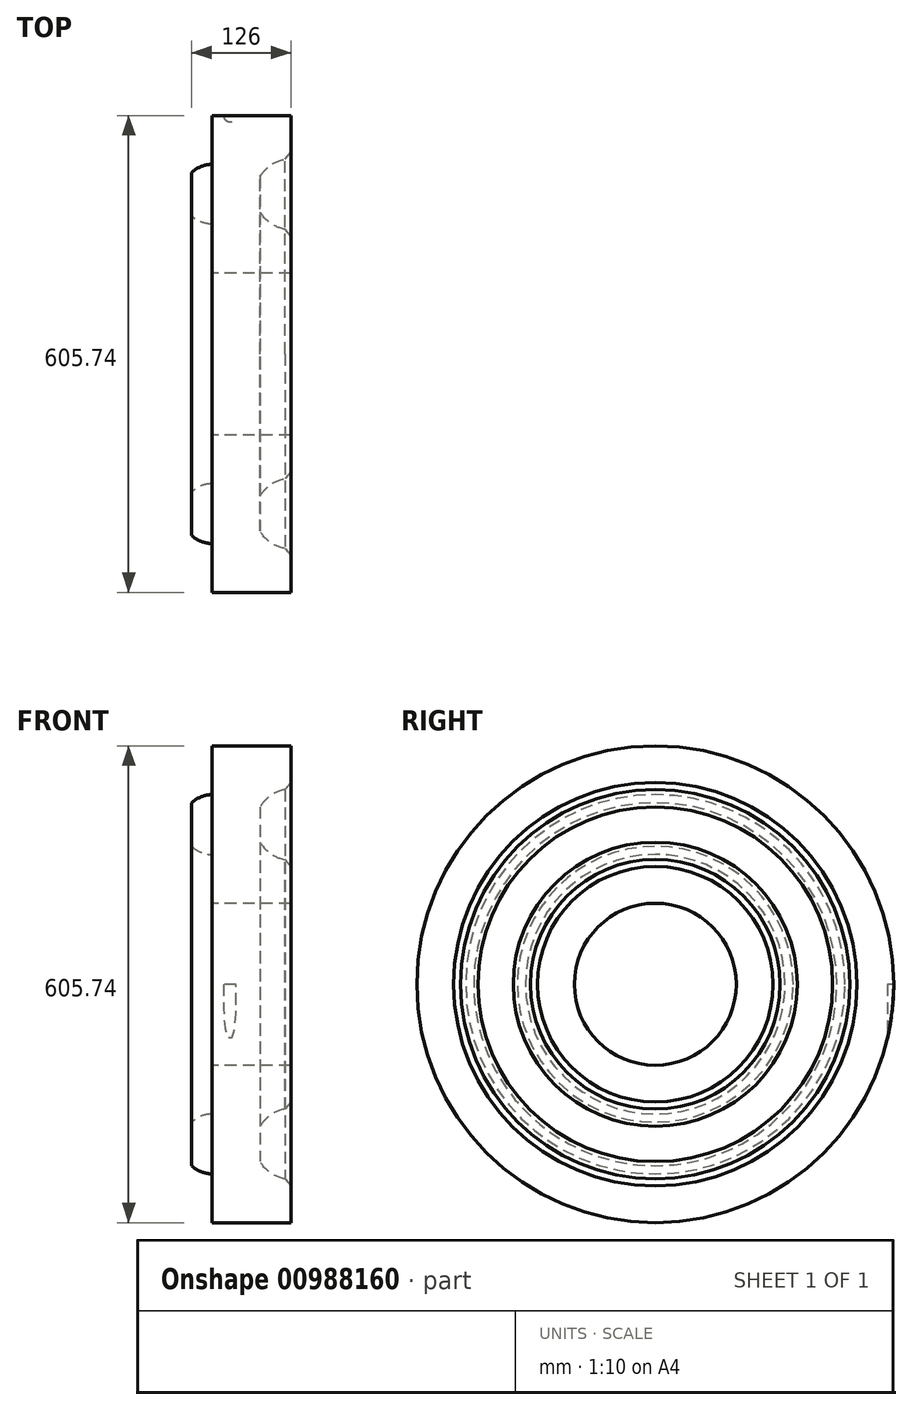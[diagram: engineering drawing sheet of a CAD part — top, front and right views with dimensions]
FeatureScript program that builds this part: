
annotation { "Feature Type Name" : "Feature", "Feature Type Description" : "" }
export const myFeature = defineFeature(function(context is Context, id is Id, definition is map)
    precondition{}
    {
        {
            var Q0;
            Q0=qCreatedBy(makeId("Top.planeOp"),FACE);
            var sketch = newSketch(context, id + "F0", { "sketchPlane" : qUnion([Q0])});
            skLineSegment(sketch, "E0", {"start": v(-458.73, 0) * mm, "end": v(0, 0) * mm, "construction": true});
            skLineSegment(sketch, "E1", {"start": v(-100, 302.87) * mm, "end": v(-100, 240.87) * mm});
            skLineSegment(sketch, "E2", {"start": v(-100, 102.87) * mm, "end": v(0, 102.87) * mm});
            skLineSegment(sketch, "E3", {"start": v(0, 102.87) * mm, "end": v(0, 157.87) * mm});
            skArc(sketch, "E4", {"start": v(-100, 164.87) * mm, "mid": v(-113.98, 167.54) * mm, "end": v(-126, 175.16) * mm});
            skLineSegment(sketch, "E5", {"start": v(-126, 230.58) * mm, "end": v(-126, 175.16) * mm});
            skArc(sketch, "E6.trimOffspring", {"start": v(-126, 230.58) * mm, "mid": v(-113.98, 238.2) * mm, "end": v(-100, 240.87) * mm});
            skLineSegment(sketch, "E7.trimOffspring", {"start": v(-100, 164.87) * mm, "end": v(-100, 102.87) * mm});
            skArc(sketch, "E8", {"start": v(-100, 164.87) * mm, "mid": v(-138, 202.87) * mm, "end": v(-100, 240.87) * mm, "construction": true});
            skLineSegment(sketch, "E9", {"start": v(-100, 202.87) * mm, "end": v(0, 202.87) * mm, "construction": true});
            skArc(sketch, "E10", {"start": v(0, 157.87) * mm, "mid": v(-22.53, 163.91) * mm, "end": v(-39, 180.42) * mm});
            skLineSegment(sketch, "E11", {"start": v(-39, 225.32) * mm, "end": v(-39, 180.42) * mm});
            skArc(sketch, "E12.trimOffspring", {"start": v(-39, 225.32) * mm, "mid": v(-22.53, 241.83) * mm, "end": v(0, 247.87) * mm});
            skLineSegment(sketch, "E13.trimOffspring", {"start": v(0, 247.87) * mm, "end": v(0, 302.87) * mm});
            skArc(sketch, "E14", {"start": v(0, 157.87) * mm, "mid": v(-45, 202.87) * mm, "end": v(0, 247.87) * mm, "construction": true});
            skLineSegment(sketch, "E15", {"start": v(-100, 302.87) * mm, "end": v(0, 302.87) * mm});
            skSolve(sketch);
        }
        {
            var Q0;
            Q0=makeQuery(id+"F0.imprint","IMPRINT",FACE,{"disambiguationData":[TD([[makeQuery(id+"F0.imprint","IMPRINT",EDGE,{"derivedFrom":sQuery(id+"F0.wireOp",EDGE,"E1")}),1.0]])]});
            var Q1;
            Q1=sQuery(id+"F0.wireOp",EDGE,"E0");
            revolve(context, id + "F1", {"surfaceOperationType" : NewSurfaceOperationType.NEW, "entities" : qUnion([Q0]), "axis" : qUnion([Q1]), "revolveType" : RevolveType.FULL});
        }
        {
            var Q0;
            Q0=makeQuery(id+"F1.opRevolve","SWEPT_EDGE",EDGE,{"disambiguationData":[OSD([sQuery(id+"F0.wireOp",EDGE,"E12.trimOffspring"),sQuery(id+"F0.wireOp",EDGE,"E13.trimOffspring")])]});
            var Q1;
            Q1=makeQuery(id+"F1.opRevolve","SWEPT_EDGE",EDGE,{"disambiguationData":[OSD([sQuery(id+"F0.wireOp",EDGE,"E3"),sQuery(id+"F0.wireOp",EDGE,"E10")])]});
            chamfer(context, id + "F2", {"entities" : qUnion([Q0, Q1]), "width" : 9 * mm, "tangentPropagation" : true});
        }
        {
            var Q0;
            Q0=qCreatedBy(makeId("Top.planeOp"),FACE);
            var sketch = newSketch(context, id + "F3", { "sketchPlane" : qUnion([Q0])});
            skLineSegment(sketch, "E16", {"start": v(-100, 302.87) * mm, "end": v(0, 302.87) * mm, "construction": true});
            skPoint(sketch, "E17", {"position": v(-50, 302.87) * mm});
            skPoint(sketch, "E18", {"position": v(-24.26, 302.87) * mm});
            skPoint(sketch, "E19", {"position": v(-77.55, 302.87) * mm});
            skSolve(sketch);
        }
        {
            var Q0;
            Q0=sQuery(id+"F3.wireOp",VERTEX,"E19");
            var Q1;
            Q1=makeQuery(id+"F1.opRevolve","SWEPT_BODY",BODY,{"disambiguationData":[OSD([sQuery(id+"F0.wireOp",EDGE,"E1"),sQuery(id+"F0.wireOp",EDGE,"E2"),sQuery(id+"F0.wireOp",EDGE,"E3"),sQuery(id+"F0.wireOp",EDGE,"E4"),sQuery(id+"F0.wireOp",EDGE,"E5"),sQuery(id+"F0.wireOp",EDGE,"E6.trimOffspring"),sQuery(id+"F0.wireOp",EDGE,"E7.trimOffspring"),sQuery(id+"F0.wireOp",EDGE,"E10"),sQuery(id+"F0.wireOp",EDGE,"E11"),sQuery(id+"F0.wireOp",EDGE,"E12.trimOffspring"),sQuery(id+"F0.wireOp",EDGE,"E13.trimOffspring"),sQuery(id+"F0.wireOp",EDGE,"E15")])]});
            hole(context, id + "F4", {"style" : HoleStyle.SIMPLE, "endStyle" : HoleEndStyle.THROUGH, "holeDiameter" : 16 * mm, "majorDiameter" : 5 * mm, "isTappedThrough" : true, "tappedDepth" : 12 * mm, "tapClearance" : 3, "locations" : qUnion([Q0]), "scope" : qUnion([Q1])});
        }
    });
